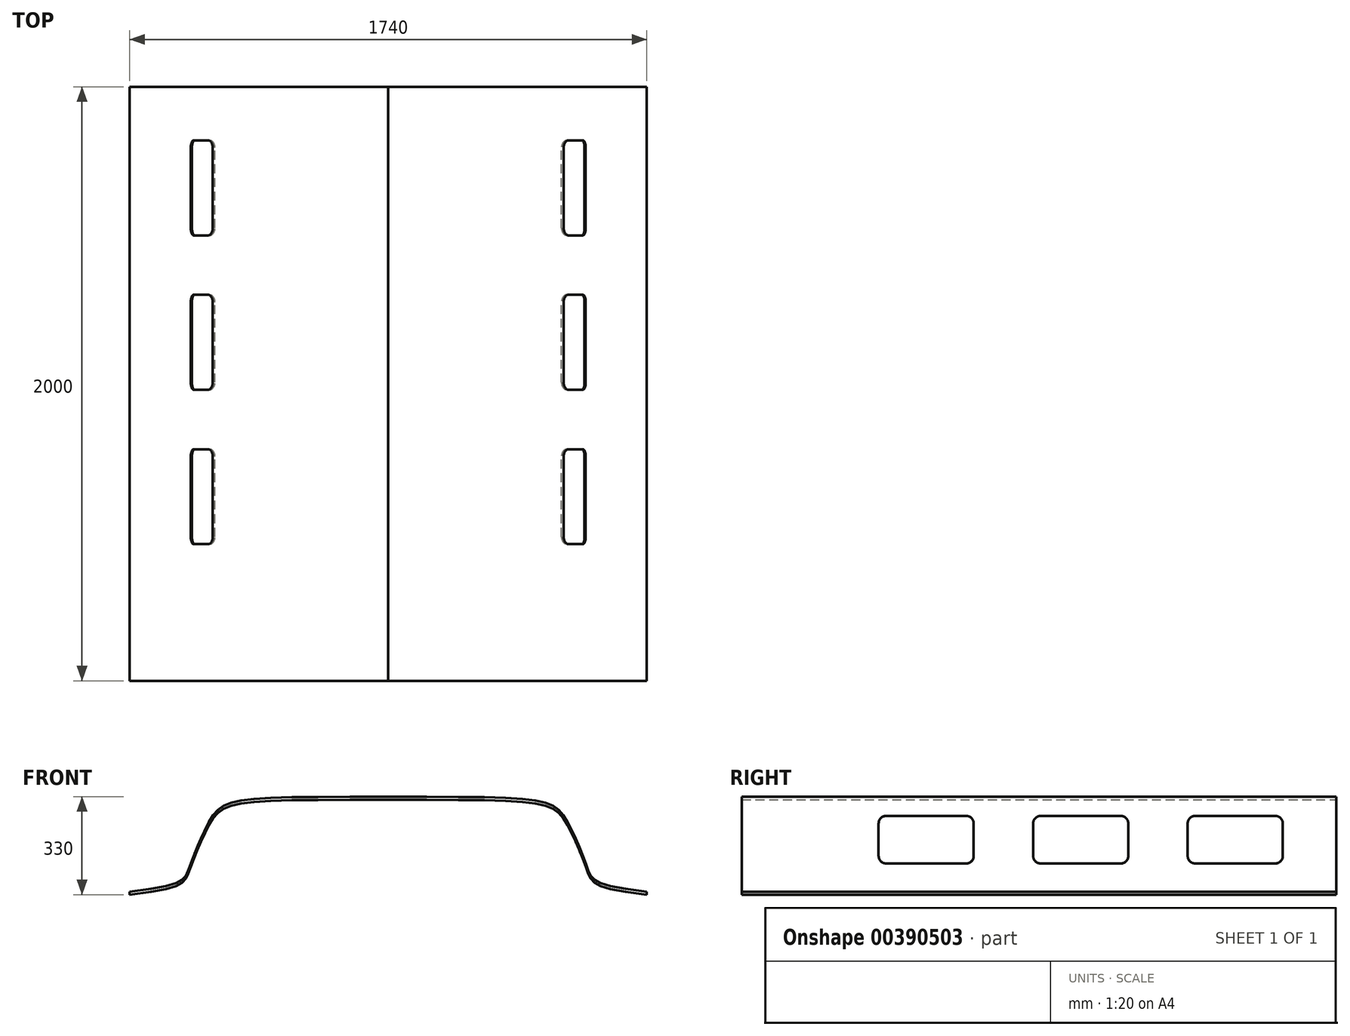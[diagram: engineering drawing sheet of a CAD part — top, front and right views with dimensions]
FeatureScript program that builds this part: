
annotation { "Feature Type Name" : "Feature", "Feature Type Description" : "" }
export const myFeature = defineFeature(function(context is Context, id is Id, definition is map)
    precondition{}
    {
        {
            var Q0;
            Q0=qCreatedBy(makeId("Right.planeOp"),FACE);
            cPlane(context, id + "F0", {"entities" : qUnion([Q0]), "cplaneType" : CPlaneType.OFFSET, "offset" : 870 * mm, "oppositeDirection" : true, "width" : 150 * mm, "height" : 150 * mm});
        }
        {
            var Q0;
            Q0=qCreatedBy(makeId("Front.planeOp"),FACE);
            var sketch = newSketch(context, id + "F1", { "sketchPlane" : qUnion([Q0])});
            skFitSpline(sketch, "E0", {"points": [v(-870, 1530) * mm, v(-670, 1610) * mm, v(-600, 1770) * mm, v(0, 1850) * mm], "startDerivative": vector(1929.5, 243.27) * mm, "endDerivative": vector(3222.18, 18.27) * mm});
            skFitSpline(sketch, "E1.MirrorCS", {"points": [v(870, 1530) * mm, v(670, 1610) * mm, v(600, 1770) * mm, v(0, 1850) * mm], "startDerivative": vector(-1929.5, 243.27) * mm, "endDerivative": vector(-3222.18, 18.27) * mm});
            skSolve(sketch);
        }
        {
            var Q0;
            Q0=qCreatedBy(id+"F0.planeOp",FACE);
            var sketch = newSketch(context, id + "F2", { "sketchPlane" : qUnion([Q0])});
            skLineSegment(sketch, "E2.bottom", {"start": v(-1000, 1530) * mm, "end": v(1000, 1530) * mm});
            skLineSegment(sketch, "E2.top", {"start": v(-1000, 1520) * mm, "end": v(1000, 1520) * mm});
            skLineSegment(sketch, "E2.left", {"start": v(-1000, 1530) * mm, "end": v(-1000, 1520) * mm});
            skLineSegment(sketch, "E2.right", {"start": v(1000, 1530) * mm, "end": v(1000, 1520) * mm});
            skSolve(sketch);
        }
        {
            var Q0;
            Q0=makeQuery(id+"F2.imprint","IMPRINT",FACE,{"disambiguationData":[TD([[makeQuery(id+"F2.imprint","IMPRINT",EDGE,{"derivedFrom":sQuery(id+"F2.wireOp",EDGE,"E2.bottom")}),-1.0]])]});
            var Q1;
            Q1=sQuery(id+"F1.wireOp",EDGE,"E1.MirrorCS");
            var Q2;
            Q2=sQuery(id+"F1.wireOp",EDGE,"E0");
            sweep(context, id + "F3", {"profiles" : qUnion([Q0]), "path" : qUnion([Q1, Q2]), "keepProfileOrientation" : true});
        }
        {
            var Q0;
            Q0=qCreatedBy(id+"F0.planeOp",FACE);
            var sketch = newSketch(context, id + "F4", { "sketchPlane" : qUnion([Q0])});
            skLineSegment(sketch, "E3.bottom", {"start": v(795, 1785) * mm, "end": v(525, 1785) * mm});
            skLineSegment(sketch, "E3.top", {"start": v(795, 1625) * mm, "end": v(525, 1625) * mm});
            skLineSegment(sketch, "E3.left", {"start": v(820, 1760) * mm, "end": v(820, 1650) * mm});
            skLineSegment(sketch, "E3.right", {"start": v(500, 1760) * mm, "end": v(500, 1650) * mm});
            skPoint(sketch, "E4.visualSharp", {"position": v(820, 1785) * mm});
            skArc(sketch, "E4.filletArc", {"start": v(820, 1760) * mm, "mid": v(812.68, 1777.68) * mm, "end": v(795, 1785) * mm});
            skPoint(sketch, "E5.visualSharp", {"position": v(820, 1625) * mm});
            skArc(sketch, "E5.filletArc", {"start": v(795, 1625) * mm, "mid": v(812.68, 1632.32) * mm, "end": v(820, 1650) * mm});
            skPoint(sketch, "E6.visualSharp", {"position": v(500, 1625) * mm});
            skArc(sketch, "E6.filletArc", {"start": v(500, 1650) * mm, "mid": v(507.32, 1632.32) * mm, "end": v(525, 1625) * mm});
            skPoint(sketch, "E7.visualSharp", {"position": v(500, 1785) * mm});
            skArc(sketch, "E7.filletArc", {"start": v(525, 1785) * mm, "mid": v(507.32, 1777.68) * mm, "end": v(500, 1760) * mm});
            skLineSegment(sketch, "E8.bottom", {"start": v(275, 1785) * mm, "end": v(5, 1785) * mm});
            skLineSegment(sketch, "E8.top", {"start": v(275, 1625) * mm, "end": v(5, 1625) * mm});
            skLineSegment(sketch, "E8.left", {"start": v(300, 1760) * mm, "end": v(300, 1650) * mm});
            skLineSegment(sketch, "E8.right", {"start": v(-20, 1760) * mm, "end": v(-20, 1650) * mm});
            skPoint(sketch, "E9.visualSharp", {"position": v(300, 1785) * mm});
            skArc(sketch, "E9.filletArc", {"start": v(300, 1760) * mm, "mid": v(292.68, 1777.68) * mm, "end": v(275, 1785) * mm});
            skPoint(sketch, "E10.visualSharp", {"position": v(300, 1625) * mm});
            skArc(sketch, "E10.filletArc", {"start": v(275, 1625) * mm, "mid": v(292.68, 1632.32) * mm, "end": v(300, 1650) * mm});
            skPoint(sketch, "E11.visualSharp", {"position": v(-20, 1625) * mm});
            skArc(sketch, "E11.filletArc", {"start": v(-20, 1650) * mm, "mid": v(-12.68, 1632.32) * mm, "end": v(5, 1625) * mm});
            skPoint(sketch, "E12.visualSharp", {"position": v(-20, 1785) * mm});
            skArc(sketch, "E12.filletArc", {"start": v(5, 1785) * mm, "mid": v(-12.68, 1777.68) * mm, "end": v(-20, 1760) * mm});
            skLineSegment(sketch, "E13.bottom", {"start": v(-245, 1785) * mm, "end": v(-515, 1785) * mm});
            skLineSegment(sketch, "E13.top", {"start": v(-245, 1625) * mm, "end": v(-515, 1625) * mm});
            skLineSegment(sketch, "E13.left", {"start": v(-220, 1760) * mm, "end": v(-220, 1650) * mm});
            skLineSegment(sketch, "E13.right", {"start": v(-540, 1760) * mm, "end": v(-540, 1650) * mm});
            skPoint(sketch, "E14.visualSharp", {"position": v(-220, 1785) * mm});
            skArc(sketch, "E14.filletArc", {"start": v(-220, 1760) * mm, "mid": v(-227.32, 1777.68) * mm, "end": v(-245, 1785) * mm});
            skPoint(sketch, "E15.visualSharp", {"position": v(-220, 1625) * mm});
            skArc(sketch, "E15.filletArc", {"start": v(-245, 1625) * mm, "mid": v(-227.32, 1632.32) * mm, "end": v(-220, 1650) * mm});
            skPoint(sketch, "E16.visualSharp", {"position": v(-540, 1625) * mm});
            skArc(sketch, "E16.filletArc", {"start": v(-540, 1650) * mm, "mid": v(-532.68, 1632.32) * mm, "end": v(-515, 1625) * mm});
            skPoint(sketch, "E17.visualSharp", {"position": v(-540, 1785) * mm});
            skArc(sketch, "E17.filletArc", {"start": v(-515, 1785) * mm, "mid": v(-532.68, 1777.68) * mm, "end": v(-540, 1760) * mm});
            skSolve(sketch);
        }
        {
            var Q0;
            Q0 = qSketchRegion(id + "F4", true);
            extrude(context, id + "F5", {"entities" : qUnion([Q0]), "operationType" : NewBodyOperationType.REMOVE, "endBound" : BoundingType.THROUGH_ALL, "depth" : 25 * mm});
        }
    });
